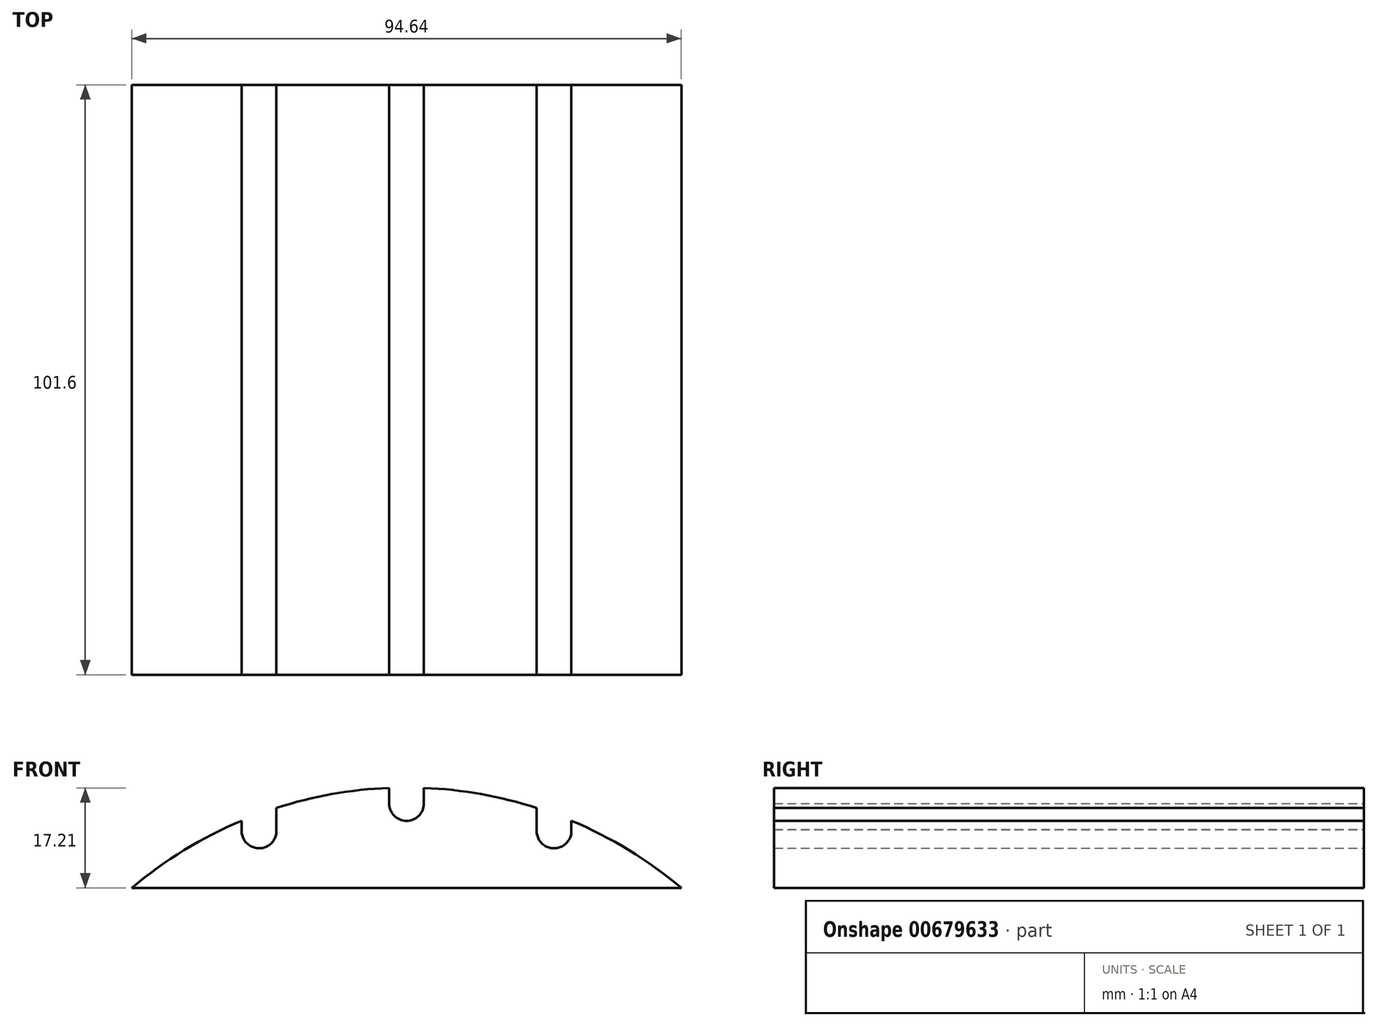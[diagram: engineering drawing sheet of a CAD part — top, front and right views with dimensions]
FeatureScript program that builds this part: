
annotation { "Feature Type Name" : "Feature", "Feature Type Description" : "" }
export const myFeature = defineFeature(function(context is Context, id is Id, definition is map)
    precondition{}
    {
        {
            var Q0;
            Q0=qCreatedBy(makeId("Front.planeOp"),FACE);
            var sketch = newSketch(context, id + "F0", { "sketchPlane" : qUnion([Q0])});
            skCircle(sketch, "E0", {"center": v(0, 0) * mm, "radius": 73.47 * mm});
            skLineSegment(sketch, "E1.bottom", {"start": v(-75.18, 56.2) * mm, "end": v(75.18, 56.2) * mm});
            skLineSegment(sketch, "E1.top", {"start": v(-75.18, -64.76) * mm, "end": v(75.18, -64.76) * mm});
            skLineSegment(sketch, "E1.left", {"start": v(-75.18, 56.2) * mm, "end": v(-75.18, -64.76) * mm});
            skLineSegment(sketch, "E1.right", {"start": v(75.18, 56.2) * mm, "end": v(75.18, -64.76) * mm});
            skCircle(sketch, "E2", {"center": v(-25.4, 66) * mm, "radius": 3 * mm});
            skCircle(sketch, "E3", {"center": v(0, 70.72) * mm, "radius": 3 * mm});
            skCircle(sketch, "E4", {"center": v(25.4, 66) * mm, "radius": 3 * mm});
            skLineSegment(sketch, "E5.bottom", {"start": v(-28.4, 66) * mm, "end": v(-22.41, 66) * mm});
            skLineSegment(sketch, "E5.top", {"start": v(-28.4, 72.13) * mm, "end": v(-22.41, 72.13) * mm});
            skLineSegment(sketch, "E5.left", {"start": v(-28.4, 66) * mm, "end": v(-28.4, 72.13) * mm});
            skLineSegment(sketch, "E5.right", {"start": v(-22.41, 66) * mm, "end": v(-22.41, 72.13) * mm});
            skLineSegment(sketch, "E6.bottom", {"start": v(3, 70.72) * mm, "end": v(-3.02, 70.72) * mm});
            skLineSegment(sketch, "E6.top", {"start": v(3, 75.98) * mm, "end": v(-3.02, 75.98) * mm});
            skLineSegment(sketch, "E6.left", {"start": v(3, 70.72) * mm, "end": v(3, 75.98) * mm});
            skLineSegment(sketch, "E6.right", {"start": v(-3.02, 70.72) * mm, "end": v(-3.02, 75.98) * mm});
            skLineSegment(sketch, "E7.bottom", {"start": v(28.4, 66) * mm, "end": v(22.4, 66) * mm});
            skLineSegment(sketch, "E7.top", {"start": v(28.4, 72.77) * mm, "end": v(22.4, 72.77) * mm});
            skLineSegment(sketch, "E7.left", {"start": v(28.4, 66) * mm, "end": v(28.4, 72.77) * mm});
            skLineSegment(sketch, "E7.right", {"start": v(22.4, 66) * mm, "end": v(22.4, 72.77) * mm});
            skLineSegment(sketch, "E8.bottom", {"start": v(-50.8, 46.04) * mm, "end": v(50.8, 46.04) * mm});
            skLineSegment(sketch, "E8.top", {"start": v(-50.8, 39.69) * mm, "end": v(50.8, 39.69) * mm});
            skLineSegment(sketch, "E8.left", {"start": v(-50.8, 46.04) * mm, "end": v(-50.8, 39.69) * mm});
            skLineSegment(sketch, "E8.right", {"start": v(50.8, 46.04) * mm, "end": v(50.8, 39.69) * mm});
            skSolve(sketch);
        }
        {
            var Q0;
            {var subQ0=sQuery(id+"F0.wireOp",EDGE,"E7.left");var subQ6=sQuery(id+"F0.wireOp",EDGE,"E0");var subQ25=makeQuery(id+"F0.imprint","INTERSECT",VERTEX,{"derivedFrom":[subQ6,subQ0]});Q0=makeQuery(id+"F0.imprint","IMPRINT",FACE,{"disambiguationData":[TD([[makeQuery(id+"F0.imprint","IMPRINT",EDGE,{"disambiguationData":[TD([[subQ25,1.0]])],"derivedFrom":subQ6}),1.0]])]});}
            extrude(context, id + "F1", {"entities" : qUnion([Q0]), "depth" : 101.6 * mm, "offsetDistance" : 25.4 * mm});
        }
    });
